# Revit family: Vitra_Plural_SlımWCSeat_(Copper) 126-003-029
name_source: partatom
category: Plumbing Fixtures
revit_build: Autodesk Revit 2017 (Build: 20160225_1515(x64)
units: mm (PartAtom-declared; Revit-internal decimal feet)

## family parameters
Cut with Voids When Loaded = No
Host = Face
OmniClass Number = 23.45.05.21
OmniClass Title = Plumbing Fixtures - Sanitary Disposal Units
Part Type = Normal
Room Calculation Point = No
Round Connector Dimension = Use Diameter
Shared = Yes

## types (5) — shared parameters
BIMobject category = Sanitary - Toilet Seats
CW Connection = No
Default Elevation = 410 mm  [stored 1.34514 ft]
Description = VitrA Plural WC Seat, Soft Closing
Design country = Turkey
HW Connection = No
IFC Classification = Sanitary Terminal
Main Material = Ceramic
Manufacturer = Vitra
Manufacturer name = Vitra
NBS Referans Code = 35-93-95
NBS Referans Description = Wc Seats And Covers
Nominal Depth (mm) = 478 mm
Nominal Height (mm) = 50 mm
Nominal Width (mm) = 366 mm
OmniClass Code = 23-31 19 19 11
OmniClass Description = Toilets
Product certification = https://vitraglobal.com
Product data url = https://www.vitra.com.tr
Product family = Plural
UNSPSC Code = 35-93-95
UNSPSC Description = Water Operated Water Closets
URL = https://www.vitra.com.tr
Uniclass 1.4 Code = L72164
Uniclass 1.4 Description = Toilets
Uniclass 2.0 Code = PR-35-93-95
Uniclass 2.0 Description = Wc Seats And Covers
Uniclass 2015 Code = Pr_40_20_93_95
Uniclass 2015 Name = WC seats and covers
Vent Connection = No
Warranty Period (Year) = 2 Years
Waste Connection = No
Weight Net (kg) = 2,20
Youtube = https://www.youtube.com
zero-valued in all types: Cost

## per-type parameters (varying)
| type | Article No. (default) | Color | Model | Product SKU | Secondary Material |
| WCSeat_Slim_Vitra_Plural_(White)_ 126-003-029 | 126-003-029 | White | 126-003-029 | 126-003-029 | Vitra-Ceramic-White |
| WCSeat_Slim_Vitra_Plural_(MatteWhite)_ 126-001-029 | 126-001-029 | Matte White | 126-001-029 | 126-001-029 | Vitra-MatteWhite |
| WCSeat_Slim_Vitra_Plural_(MatteBeige)_ 126-020-029 | 126-020-029 | Matte Beige | 126-020-029 | 126-020-029 | Vitra-MatteBeige |
| WCSeat_Slim_Vitra_Plural_(MatteMink)_ 126-050-029 | 126-050-029 | Matte Mink | 126-050-029 | 126-050-029 | Vitra-MatteMink |
| WCSeat_Slim_Vitra_Plural_(MatteBlack)_ 126-083-029 | 126-083-029 | Matte Black | 126-083-029 | 126-083-029 | Vitra-MatteBlack |

note: [stored X ft] marks values corroborated as IEEE doubles in the binary element streams (Revit-internal decimal feet)

## geometry (parser evidence)
native form markers: Sweep x3
no freeform markers — native parametric forms only
